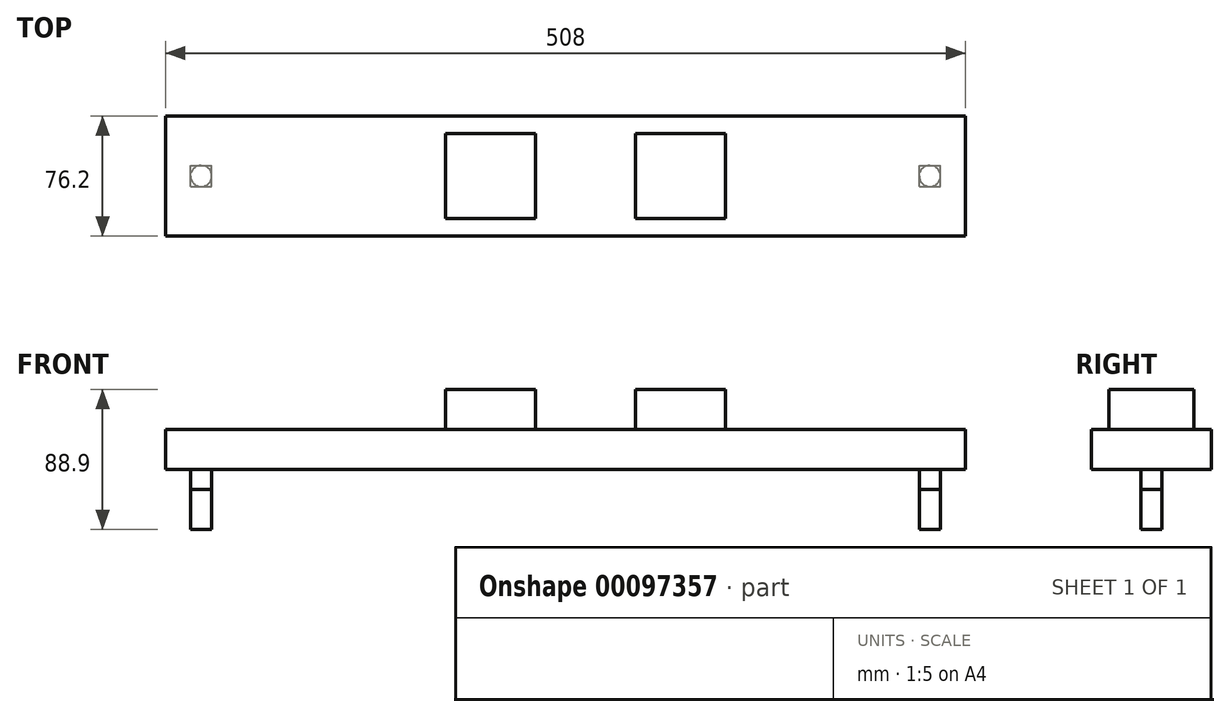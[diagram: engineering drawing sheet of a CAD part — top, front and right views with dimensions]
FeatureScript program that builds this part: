
annotation { "Feature Type Name" : "Feature", "Feature Type Description" : "" }
export const myFeature = defineFeature(function(context is Context, id is Id, definition is map)
    precondition{}
    {
        {
            var Q0;
            Q0=qCreatedBy(makeId("Front.planeOp"),FACE);
            var sketch = newSketch(context, id + "F0", { "sketchPlane" : qUnion([Q0])});
            skLineSegment(sketch, "E0.bottom", {"start": v(-254, 12.7) * mm, "end": v(254, 12.7) * mm});
            skLineSegment(sketch, "E0.top", {"start": v(-254, -12.7) * mm, "end": v(254, -12.7) * mm});
            skLineSegment(sketch, "E0.left", {"start": v(-254, 12.7) * mm, "end": v(-254, -12.7) * mm});
            skLineSegment(sketch, "E0.right", {"start": v(254, 12.7) * mm, "end": v(254, -12.7) * mm});
            skSolve(sketch);
        }
        {
            var Q0;
            Q0 = qSketchRegion(id + "F0", true);
            extrude(context, id + "F1", {"entities" : qUnion([Q0]), "endBound" : BoundingType.SYMMETRIC, "depth" : 76.2 * mm});
        }
        {
            var Q0;
            Q0=makeQuery(id+"F1.opExtrude","SWEPT_FACE",FACE,{"disambiguationData":[OSD([sQuery(id+"F0.wireOp",EDGE,"E0.top")])]});
            var sketch = newSketch(context, id + "F2", { "sketchPlane" : qUnion([Q0])});
            skLineSegment(sketch, "E1.bottom", {"start": v(-238.12, 6.73) * mm, "end": v(-224.65, 6.73) * mm});
            skLineSegment(sketch, "E1.top", {"start": v(-238.12, -6.74) * mm, "end": v(-224.65, -6.74) * mm});
            skLineSegment(sketch, "E1.left", {"start": v(-238.12, 6.73) * mm, "end": v(-238.12, -6.74) * mm});
            skLineSegment(sketch, "E1.right", {"start": v(-224.65, 6.73) * mm, "end": v(-224.65, -6.74) * mm});
            skLineSegment(sketch, "E2.bottom", {"start": v(224.65, 6.73) * mm, "end": v(238.13, 6.73) * mm});
            skLineSegment(sketch, "E2.top", {"start": v(224.65, -6.74) * mm, "end": v(238.13, -6.74) * mm});
            skLineSegment(sketch, "E2.left", {"start": v(224.65, 6.73) * mm, "end": v(224.65, -6.74) * mm});
            skLineSegment(sketch, "E2.right", {"start": v(238.13, 6.73) * mm, "end": v(238.13, -6.74) * mm});
            skSolve(sketch);
        }
        {
            var Q0;
            Q0 = qSketchRegion(id + "F2", true);
            extrude(context, id + "F3", {"entities" : qUnion([Q0]), "operationType" : NewBodyOperationType.ADD, "depth" : 12.7 * mm});
        }
        {
            var Q0;
            Q0=makeQuery(id+"F1.opExtrude","SWEPT_FACE",FACE,{"disambiguationData":[OSD([sQuery(id+"F0.wireOp",EDGE,"E0.bottom")])]});
            var sketch = newSketch(context, id + "F4", { "sketchPlane" : qUnion([Q0])});
            skLineSegment(sketch, "E3.bottom", {"start": v(-76.2, 26.99) * mm, "end": v(-19.05, 26.99) * mm});
            skLineSegment(sketch, "E3.top", {"start": v(-76.2, -26.99) * mm, "end": v(-19.05, -26.99) * mm});
            skLineSegment(sketch, "E3.left", {"start": v(-76.2, 26.99) * mm, "end": v(-76.2, -26.99) * mm});
            skLineSegment(sketch, "E3.right", {"start": v(-19.05, 26.99) * mm, "end": v(-19.05, -26.99) * mm});
            skLineSegment(sketch, "E4.bottom", {"start": v(44.45, 27) * mm, "end": v(101.6, 27) * mm});
            skLineSegment(sketch, "E4.top", {"start": v(44.45, -26.97) * mm, "end": v(101.6, -26.97) * mm});
            skLineSegment(sketch, "E4.left", {"start": v(44.45, 27) * mm, "end": v(44.45, -26.97) * mm});
            skLineSegment(sketch, "E4.right", {"start": v(101.6, 27) * mm, "end": v(101.6, -26.97) * mm});
            skSolve(sketch);
        }
        {
            var Q0;
            Q0 = qSketchRegion(id + "F4", true);
            extrude(context, id + "F5", {"entities" : qUnion([Q0]), "operationType" : NewBodyOperationType.ADD, "depth" : 25.4 * mm});
        }
        {
            var Q0;
            Q0=makeQuery(id+"F3.opExtrude","CAP_FACE",FACE,{"disambiguationData":[OSD([sQuery(id+"F2.wireOp",EDGE,"E1.bottom"),sQuery(id+"F2.wireOp",EDGE,"E1.top"),sQuery(id+"F2.wireOp",EDGE,"E1.left"),sQuery(id+"F2.wireOp",EDGE,"E1.right")])],"isStart":false});
            var sketch = newSketch(context, id + "F6", { "sketchPlane" : qUnion([Q0])});
            skCircle(sketch, "E5", {"center": v(-231.4, 0) * mm, "radius": 6.73 * mm});
            skCircle(sketch, "E6.MirrorC", {"center": v(231.4, 0) * mm, "radius": 6.73 * mm});
            skSolve(sketch);
        }
        {
            var Q0;
            Q0 = qSketchRegion(id + "F6", true);
            extrude(context, id + "F7", {"entities" : qUnion([Q0]), "operationType" : NewBodyOperationType.ADD, "depth" : 25.4 * mm});
        }
    });
